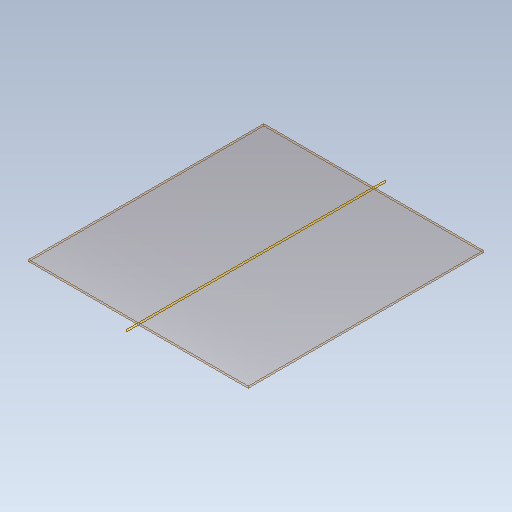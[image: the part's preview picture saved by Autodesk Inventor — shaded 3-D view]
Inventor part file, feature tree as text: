
AUTODESK INVENTOR PART (.ipt)
format: ipt  version: 2020.2 (Build 242310000, 310)  size: 91,136 bytes
history: native  units: in
note: dims shown in document units (in); Inventor stores cm internally (conversion verified against a paired STEP export)
features: extrude x1, sketch x1
ambient origin geometry x8: Origin, YZ Plane, XZ Plane, XY Plane, X Axis, Y Axis, Z Axis, Center Point
bodies: Solid1 (feature_tree)
feature tree (2):
  extrude  "Extrusion1"  Depth=28.0in
  sketch  "Sketch1"  dims[d0=0.25in d1=0.0in d2=28.0in d3=30.0in]
